# Revit family: Drain_Floor_Round-Zurn-Z415N
name_source: partatom
category: Plumbing Fixtures
units: mm (PartAtom-declared; Revit-internal decimal feet)

## family parameters
Always vertical = Yes
Cut with Voids When Loaded = No
Maintain Annotation Orientation = No
OmniClass Number = 23.70.50.21.24.14
OmniClass Title = Deck Waste Water Drains
Part Type = Normal
Room Calculation Point = No
Round Connector Dimension = Use Radius
Shared = No
Work Plane-Based = No

## types (57) — shared parameters
Assembly Code = D2030300
Body radius OD = 4.175 "
CW Connection = No
Default Elevation = 20 "
Description = BODY ASSEMBLY W/ “TYPE I” STRAINER
HW Connection = No
Manufacturer = Zurn Water, LLC
Manufacurer Brand = Zurn
Material Main = Iron - Zurn - Cast - Painted - Blue
Modified Date = 12/05/2025
Product Documentation Link = https://files.zurn.com
Product Installation Sheet URL = https://files.zurn.com
Product Page URL = https://www.zurn.com
Product data url = https://www.bimobject.com
URL = www.zurn.com
Vent Connection = No
Waste Connection = Yes
zero-valued in all types: CWFU, HWFU, WFU

## per-type parameters (varying)
| type | Approx. Wt. Lbs. | Body Height (E) | Grate Radius | Model | Pipe Size 'A' (Inner Diameter) | Pipe Size 'A' (Inner Radius) | Pipe Size 'A' (Nominal Diameter) | Pipe Size 'A' (Nominal Radius) | Pipe Size 'A' (Outer Diameter) | Pipe Size 'A' (Outer Radius) | Strainer Diameter (B) | Strainer Material | Strainer Open Area | Strainer Top Size 7" | Strainer Top Size 9" | Type Comments |
| Z415N-2IP-7B | 17.00 lb | 2.438 " | 3.2 " | Z415N | 2.067 " | 1.034 " | 2 " | 1 " | 2.375 " | 1.188 " | 7 " | Iron - Zurn - Cast - Painted - Blue | 12 in² | Yes | No | Z415N with 7 Inch Strainer and 2 Inch IP Threaded Outlet |
| Z415N-2IP-9B | 21.00 lb | 2.438 " | 4.2 " | Z415N | 2.067 " | 1.034 " | 2 " | 1 " | 2.375 " | 1.188 " | 9 " | Iron - Zurn - Cast - Painted - Blue | 23 in² | No | Yes | Z415N with 9 Inch Strainer and 2 Inch IP Threaded Outlet |
| Z415N-2NH-7B | 17.00 lb | 3.183 " | 3.2 " | Z415N | 2.067 " | 1.034 " | 2 " | 1 " | 2.375 " | 1.188 " | 7 " | Iron - Zurn - Cast - Painted - Blue | 12 in² | Yes | No | Z415N with 7 Inch Strainer and 2 Inch No-Hub Outlet |
| Z415N-2NH-9B | 21.00 lb | 3.183 " | 4.2 " | Z415N | 2.067 " | 1.034 " | 2 " | 1 " | 2.375 " | 1.188 " | 9 " | Iron - Zurn - Cast - Painted - Blue | 23 in² | No | Yes | Z415N with 9 Inch Strainer and 2 Inch No-Hub Outlet |
| Z415N-2NL-7B | 17.00 lb | 3.875 " | 3.2 " | Z415N | 2.067 " | 1.034 " | 2 " | 1 " | 2.375 " | 1.188 " | 7 " | Iron - Zurn - Cast - Painted - Blue | 12 in² | Yes | No | Z415N with 7 Inch Strainer and 2 Inch Neo-Lock Outlet |
| Z415N-2NL-9B | 21.00 lb | 3.875 " | 4.2 " | Z415N | 2.067 " | 1.034 " | 2 " | 1 " | 2.375 " | 1.188 " | 9 " | Iron - Zurn - Cast - Painted - Blue | 23 in² | No | Yes | Z415N with 9 Inch Strainer and 2 Inch Neo-Lock Outlet |
| Z415N-3IP-7B | 17.00 lb | 2.75 " | 3.2 " | Z415N | 3.026 " | 1.513 " | 3 " | 1.5 " | 3.5 " | 1.75 " | 7 " | Iron - Zurn - Cast - Painted - Blue | 12 in² | Yes | No | Z415N with 7 Inch Strainer and 3 Inch IP Threaded Outlet |
| Z415N-3IP-9B | 21.00 lb | 2.75 " | 4.2 " | Z415N | 3.026 " | 1.513 " | 3 " | 1.5 " | 3.5 " | 1.75 " | 9 " | Iron - Zurn - Cast - Painted - Blue | 23 in² | No | Yes | Z415N with 9 Inch Strainer and 3 Inch IP Threaded Outlet |
| Z415N-3NH-7B | 17.00 lb | 3.183 " | 3.2 " | Z415N | 3.026 " | 1.513 " | 3 " | 1.5 " | 3.5 " | 1.75 " | 7 " | Iron - Zurn - Cast - Painted - Blue | 12 in² | Yes | No | Z415N with 7 Inch Strainer and 3 Inch No-Hub Outlet |
| Z415N-3NH-9B | 21.00 lb | 3.183 " | 4.2 " | Z415N | 3.026 " | 1.513 " | 3 " | 1.5 " | 3.5 " | 1.75 " | 9 " | Iron - Zurn - Cast - Painted - Blue | 23 in² | No | Yes | Z415N with 9 Inch Strainer and 3 Inch No-Hub Outlet |
| Z415N-3NL-7B | 17.00 lb | 3.875 " | 3.2 " | Z415N | 3.026 " | 1.513 " | 3 " | 1.5 " | 3.5 " | 1.75 " | 7 " | Iron - Zurn - Cast - Painted - Blue | 12 in² | Yes | No | Z415N with 7 Inch Strainer and 3 Inch Neo-Lock Outlet |
| Z415N-3NL-9B | 21.00 lb | 3.875 " | 4.2 " | Z415N | 3.026 " | 1.513 " | 3 " | 1.5 " | 3.5 " | 1.75 " | 9 " | Iron - Zurn - Cast - Painted - Blue | 23 in² | No | Yes | Z415N with 9 Inch Strainer and 3 Inch Neo-Lock Outlet |
| Z415N-4IP-7B | 17.00 lb | 2.813 " | 3.2 " | Z415N | 4.028 " | 2.014 " | 4 " | 2 " | 4.5 " | 2.25 " | 7 " | Iron - Zurn - Cast - Painted - Blue | 12 in² | Yes | No | Z415N with 7 Inch Strainer and 4 Inch IP Threaded Outlet |
| Z415N-4IP-9B | 21.00 lb | 2.813 " | 4.2 " | Z415N | 4.028 " | 2.014 " | 4 " | 2 " | 4.5 " | 2.25 " | 9 " | Iron - Zurn - Cast - Painted - Blue | 23 in² | No | Yes | Z415N with 9 Inch Strainer and 4 Inch IP Threaded Outlet |
| Z415N-4NH-7B | 17.00 lb | 3.183 " | 3.2 " | Z415N | 4.028 " | 2.014 " | 4 " | 2 " | 4.5 " | 2.25 " | 7 " | Iron - Zurn - Cast - Painted - Blue | 12 in² | Yes | No | Z415N with 7 Inch Strainer and 4 Inch No-Hub Outlet |
| Z415N-4NH-9B | 21.00 lb | 3.183 " | 4.2 " | Z415N | 4.028 " | 2.014 " | 4 " | 2 " | 4.5 " | 2.25 " | 9 " | Iron - Zurn - Cast - Painted - Blue | 23 in² | No | Yes | Z415N with 9 Inch Strainer and 4 Inch No-Hub Outlet |
| Z415N-4NL-7B | 17.00 lb | 3.875 " | 3.2 " | Z415N | 4.028 " | 2.014 " | 4 " | 2 " | 4.5 " | 2.25 " | 7 " | Iron - Zurn - Cast - Painted - Blue | 12 in² | Yes | No | Z415N with 7 Inch Strainer and 4 Inch Neo-Lock Outlet |
| Z415N-4NL-9B | 21.00 lb | 3.875 " | 4.2 " | Z415N | 4.028 " | 2.014 " | 4 " | 2 " | 4.5 " | 2.25 " | 9 " | Iron - Zurn - Cast - Painted - Blue | 23 in² | No | Yes | Z415N with 9 Inch Strainer and 4 Inch Neo-Lock Outlet |
| Z415N-6IP-9B | 23.00 lb | 2.875 " | 4.2 " | Z415N | 6.065 " | 3.033 " | 6 " | 3 " | 6.625 " | 3.313 " | 9 " | Iron - Zurn - Cast - Painted - Blue | 23 in² | No | Yes | Z415N with 9 Inch Strainer and 6 Inch IP Threaded Outlet |
| ZB415N-2IP-7B | 17.00 lb | 2.438 " | 3.2 " | ZB415N | 2.067 " | 1.034 " | 2 " | 1 " | 2.375 " | 1.188 " | 7 " | Bronze - Zurn - Polished | 12 in² | Yes | No | ZB415N with 7 Inch Strainer and 2 Inch IP Threaded Outlet |
| ZB415N-2IP-9B | 21.00 lb | 2.438 " | 4.2 " | ZB415N | 2.067 " | 1.034 " | 2 " | 1 " | 2.375 " | 1.188 " | 9 " | Bronze - Zurn - Polished | 23 in² | No | Yes | ZB415N with 9 Inch Strainer and 2 Inch IP Threaded Outlet |
| ZB415N-2NH-7B | 17.00 lb | 3.183 " | 3.2 " | ZB415N | 2.067 " | 1.034 " | 2 " | 1 " | 2.375 " | 1.188 " | 7 " | Bronze - Zurn - Polished | 12 in² | Yes | No | ZB415N with 7 Inch Strainer and 2 Inch No-Hub Outlet |
| ZB415N-2NH-9B | 21.00 lb | 3.183 " | 4.2 " | ZB415N | 2.067 " | 1.034 " | 2 " | 1 " | 2.375 " | 1.188 " | 9 " | Bronze - Zurn - Polished | 23 in² | No | Yes | ZB415N with 9 Inch Strainer and 2 Inch No-Hub Outlet |
| ZB415N-2NL-7B | 17.00 lb | 3.875 " | 3.2 " | ZB415N | 2.067 " | 1.034 " | 2 " | 1 " | 2.375 " | 1.188 " | 7 " | Bronze - Zurn - Polished | 12 in² | Yes | No | ZB415N with 7 Inch Strainer and 2 Inch Neo-Lock Outlet |
| ZB415N-2NL-9B | 21.00 lb | 3.875 " | 4.2 " | ZB415N | 2.067 " | 1.034 " | 2 " | 1 " | 2.375 " | 1.188 " | 9 " | Bronze - Zurn - Polished | 23 in² | No | Yes | ZB415N with 9 Inch Strainer and 2 Inch Neo-Lock Outlet |
| ZB415N-3IP-7B | 17.00 lb | 2.75 " | 3.2 " | ZB415N | 3.026 " | 1.513 " | 3 " | 1.5 " | 3.5 " | 1.75 " | 7 " | Bronze - Zurn - Polished | 12 in² | Yes | No | ZB415N with 7 Inch Strainer and 3 Inch IP Threaded Outlet |
| ZB415N-3IP-9B | 21.00 lb | 2.75 " | 4.2 " | ZB415N | 3.026 " | 1.513 " | 3 " | 1.5 " | 3.5 " | 1.75 " | 9 " | Bronze - Zurn - Polished | 23 in² | No | Yes | ZB415N with 9 Inch Strainer and 3 Inch IP Threaded Outlet |
| ZB415N-3NH-7B | 17.00 lb | 3.183 " | 3.2 " | ZB415N | 3.026 " | 1.513 " | 3 " | 1.5 " | 3.5 " | 1.75 " | 7 " | Bronze - Zurn - Polished | 12 in² | Yes | No | ZB415N with 7 Inch Strainer and 3 Inch No-Hub Outlet |
| ZB415N-3NH-9B | 21.00 lb | 3.183 " | 4.2 " | ZB415N | 3.026 " | 1.513 " | 3 " | 1.5 " | 3.5 " | 1.75 " | 9 " | Bronze - Zurn - Polished | 23 in² | No | Yes | ZB415N with 9 Inch Strainer and 3 Inch No-Hub Outlet |
| ZB415N-3NL-7B | 17.00 lb | 3.875 " | 3.2 " | ZB415N | 3.026 " | 1.513 " | 3 " | 1.5 " | 3.5 " | 1.75 " | 7 " | Bronze - Zurn - Polished | 12 in² | Yes | No | ZB415N with 7 Inch Strainer and 3 Inch Neo-Lock Outlet |
| ZB415N-3NL-9B | 21.00 lb | 3.875 " | 4.2 " | ZB415N | 3.026 " | 1.513 " | 3 " | 1.5 " | 3.5 " | 1.75 " | 9 " | Bronze - Zurn - Polished | 23 in² | No | Yes | ZB415N with 9 Inch Strainer and 3 Inch Neo-Lock Outlet |
| ZB415N-4IP-7B | 17.00 lb | 2.813 " | 3.2 " | ZB415N | 4.028 " | 2.014 " | 4 " | 2 " | 4.5 " | 2.25 " | 7 " | Bronze - Zurn - Polished | 12 in² | Yes | No | ZB415N with 7 Inch Strainer and 4 Inch IP Threaded Outlet |
| ZB415N-4IP-9B | 21.00 lb | 2.813 " | 4.2 " | ZB415N | 4.028 " | 2.014 " | 4 " | 2 " | 4.5 " | 2.25 " | 9 " | Bronze - Zurn - Polished | 23 in² | No | Yes | ZB415N with 9 Inch Strainer and 4 Inch IP Threaded Outlet |
| ZB415N-4NH-7B | 17.00 lb | 3.183 " | 3.2 " | ZB415N | 4.028 " | 2.014 " | 4 " | 2 " | 4.5 " | 2.25 " | 7 " | Bronze - Zurn - Polished | 12 in² | Yes | No | ZB415N with 7 Inch Strainer and 4 Inch No-Hub Outlet |
| ZB415N-4NH-9B | 21.00 lb | 3.183 " | 4.2 " | ZB415N | 4.028 " | 2.014 " | 4 " | 2 " | 4.5 " | 2.25 " | 9 " | Bronze - Zurn - Polished | 23 in² | No | Yes | ZB415N with 9 Inch Strainer and 4 Inch No-Hub Outlet |
| ZB415N-4NL-7B | 17.00 lb | 3.875 " | 3.2 " | ZB415N | 4.028 " | 2.014 " | 4 " | 2 " | 4.5 " | 2.25 " | 7 " | Bronze - Zurn - Polished | 12 in² | Yes | No | ZB415N with 7 Inch Strainer and 4 Inch Neo-Lock Outlet |
| ZB415N-4NL-9B | 21.00 lb | 3.875 " | 4.2 " | ZB415N | 4.028 " | 2.014 " | 4 " | 2 " | 4.5 " | 2.25 " | 9 " | Bronze - Zurn - Polished | 23 in² | No | Yes | ZB415N with 9 Inch Strainer and 4 Inch Neo-Lock Outlet |
| ZB415N-6IP-9B | 23.00 lb | 2.875 " | 4.2 " | ZB415N | 6.065 " | 3.033 " | 6 " | 3 " | 6.625 " | 3.313 " | 9 " | Bronze - Zurn - Polished | 23 in² | No | Yes | ZB415N with 9 Inch Strainer and 6 Inch IP Threaded Outlet |
| ZN415N-2IP-7B | 17.00 lb | 2.438 " | 3.2 " | ZN415N | 2.067 " | 1.034 " | 2 " | 1 " | 2.375 " | 1.188 " | 7 " | Bronze - Zurn - Polished Nickel | 12 in² | Yes | No | ZN415N with 7 Inch Strainer and 2 Inch IP Threaded Outlet |
| ZN415N-2IP-9B | 21.00 lb | 2.438 " | 4.2 " | ZN415N | 2.067 " | 1.034 " | 2 " | 1 " | 2.375 " | 1.188 " | 9 " | Bronze - Zurn - Polished Nickel | 23 in² | No | Yes | ZN415N with 9 Inch Strainer and 2 Inch IP Threaded Outlet |
| ZN415N-2NH-7B | 17.00 lb | 3.183 " | 3.2 " | ZN415N | 2.067 " | 1.034 " | 2 " | 1 " | 2.375 " | 1.188 " | 7 " | Bronze - Zurn - Polished Nickel | 12 in² | Yes | No | ZN415N with 7 Inch Strainer and 2 Inch No-Hub Outlet |
| ZN415N-2NH-9B | 21.00 lb | 3.183 " | 4.2 " | ZN415N | 2.067 " | 1.034 " | 2 " | 1 " | 2.375 " | 1.188 " | 9 " | Bronze - Zurn - Polished Nickel | 23 in² | No | Yes | ZN415N with 9 Inch Strainer and 2 Inch No-Hub Outlet |
| ZN415N-2NL-7B | 17.00 lb | 3.875 " | 3.2 " | ZN415N | 2.067 " | 1.034 " | 2 " | 1 " | 2.375 " | 1.188 " | 7 " | Bronze - Zurn - Polished Nickel | 12 in² | Yes | No | ZN415N with 7 Inch Strainer and 2 Inch Neo-Lock Outlet |
| ZN415N-2NL-9B | 21.00 lb | 3.875 " | 4.2 " | ZN415N | 2.067 " | 1.034 " | 2 " | 1 " | 2.375 " | 1.188 " | 9 " | Bronze - Zurn - Polished Nickel | 23 in² | No | Yes | ZN415N with 9 Inch Strainer and 2 Inch Neo-Lock Outlet |
| ZN415N-3IP-7B | 17.00 lb | 2.75 " | 3.2 " | ZN415N | 3.026 " | 1.513 " | 3 " | 1.5 " | 3.5 " | 1.75 " | 7 " | Bronze - Zurn - Polished Nickel | 12 in² | Yes | No | ZN415N with 7 Inch Strainer and 3 Inch IP Threaded Outlet |
| ZN415N-3IP-9B | 21.00 lb | 2.75 " | 4.2 " | ZN415N | 3.026 " | 1.513 " | 3 " | 1.5 " | 3.5 " | 1.75 " | 9 " | Bronze - Zurn - Polished Nickel | 23 in² | No | Yes | ZN415N with 9 Inch Strainer and 3 Inch IP Threaded Outlet |
| ZN415N-3NH-7B | 17.00 lb | 3.183 " | 3.2 " | ZN415N | 3.026 " | 1.513 " | 3 " | 1.5 " | 3.5 " | 1.75 " | 7 " | Bronze - Zurn - Polished Nickel | 12 in² | Yes | No | ZN415N with 7 Inch Strainer and 3 Inch No-Hub Outlet |
| ZN415N-3NH-9B | 21.00 lb | 3.183 " | 4.2 " | ZN415N | 3.026 " | 1.513 " | 3 " | 1.5 " | 3.5 " | 1.75 " | 9 " | Bronze - Zurn - Polished Nickel | 23 in² | No | Yes | ZN415N with 9 Inch Strainer and 3 Inch No-Hub Outlet |
| ZN415N-3NL-7B | 17.00 lb | 3.875 " | 3.2 " | ZN415N | 3.026 " | 1.513 " | 3 " | 1.5 " | 3.5 " | 1.75 " | 7 " | Bronze - Zurn - Polished Nickel | 12 in² | Yes | No | ZN415N with 7 Inch Strainer and 3 Inch Neo-Lock Outlet |
| ZN415N-3NL-9B | 21.00 lb | 3.875 " | 4.2 " | ZN415N | 3.026 " | 1.513 " | 3 " | 1.5 " | 3.5 " | 1.75 " | 9 " | Bronze - Zurn - Polished Nickel | 23 in² | No | Yes | ZN415N with 9 Inch Strainer and 3 Inch Neo-Lock Outlet |
| ZN415N-4IP-7B | 17.00 lb | 2.813 " | 3.2 " | ZN415N | 4.028 " | 2.014 " | 4 " | 2 " | 4.5 " | 2.25 " | 7 " | Bronze - Zurn - Polished Nickel | 12 in² | Yes | No | ZN415N with 7 Inch Strainer and 4 Inch IP Threaded Outlet |
| ZN415N-4IP-9B | 21.00 lb | 2.813 " | 4.2 " | ZN415N | 4.028 " | 2.014 " | 4 " | 2 " | 4.5 " | 2.25 " | 9 " | Bronze - Zurn - Polished Nickel | 23 in² | No | Yes | ZN415N with 9 Inch Strainer and 4 Inch IP Threaded Outlet |
| ZN415N-4NH-7B | 17.00 lb | 3.183 " | 3.2 " | ZN415N | 4.028 " | 2.014 " | 4 " | 2 " | 4.5 " | 2.25 " | 7 " | Bronze - Zurn - Polished Nickel | 12 in² | Yes | No | ZN415N with 7 Inch Strainer and 4 Inch No-Hub Outlet |
| ZN415N-4NH-9B | 21.00 lb | 3.183 " | 4.2 " | ZN415N | 4.028 " | 2.014 " | 4 " | 2 " | 4.5 " | 2.25 " | 9 " | Bronze - Zurn - Polished Nickel | 23 in² | No | Yes | ZN415N with 9 Inch Strainer and 4 Inch No-Hub Outlet |
| ZN415N-4NL-7B | 17.00 lb | 3.875 " | 3.2 " | ZN415N | 4.028 " | 2.014 " | 4 " | 2 " | 4.5 " | 2.25 " | 7 " | Bronze - Zurn - Polished Nickel | 12 in² | Yes | No | ZN415N with 7 Inch Strainer and 4 Inch Neo-Lock Outlet |
| ZN415N-4NL-9B | 21.00 lb | 3.875 " | 4.2 " | ZN415N | 4.028 " | 2.014 " | 4 " | 2 " | 4.5 " | 2.25 " | 9 " | Bronze - Zurn - Polished Nickel | 23 in² | No | Yes | ZN415N with 9 Inch Strainer and 4 Inch Neo-Lock Outlet |
| ZN415N-6IP-9B | 23.00 lb | 2.875 " | 4.2 " | ZN415N | 6.065 " | 3.033 " | 6 " | 3 " | 6.625 " | 3.313 " | 9 " | Bronze - Zurn - Polished Nickel | 23 in² | No | Yes | ZN415N with 9 Inch Strainer and 6 Inch IP Threaded Outlet |

## geometry (parser evidence)
native form markers: Blend x4, Sweep x4
no freeform markers — native parametric forms only
